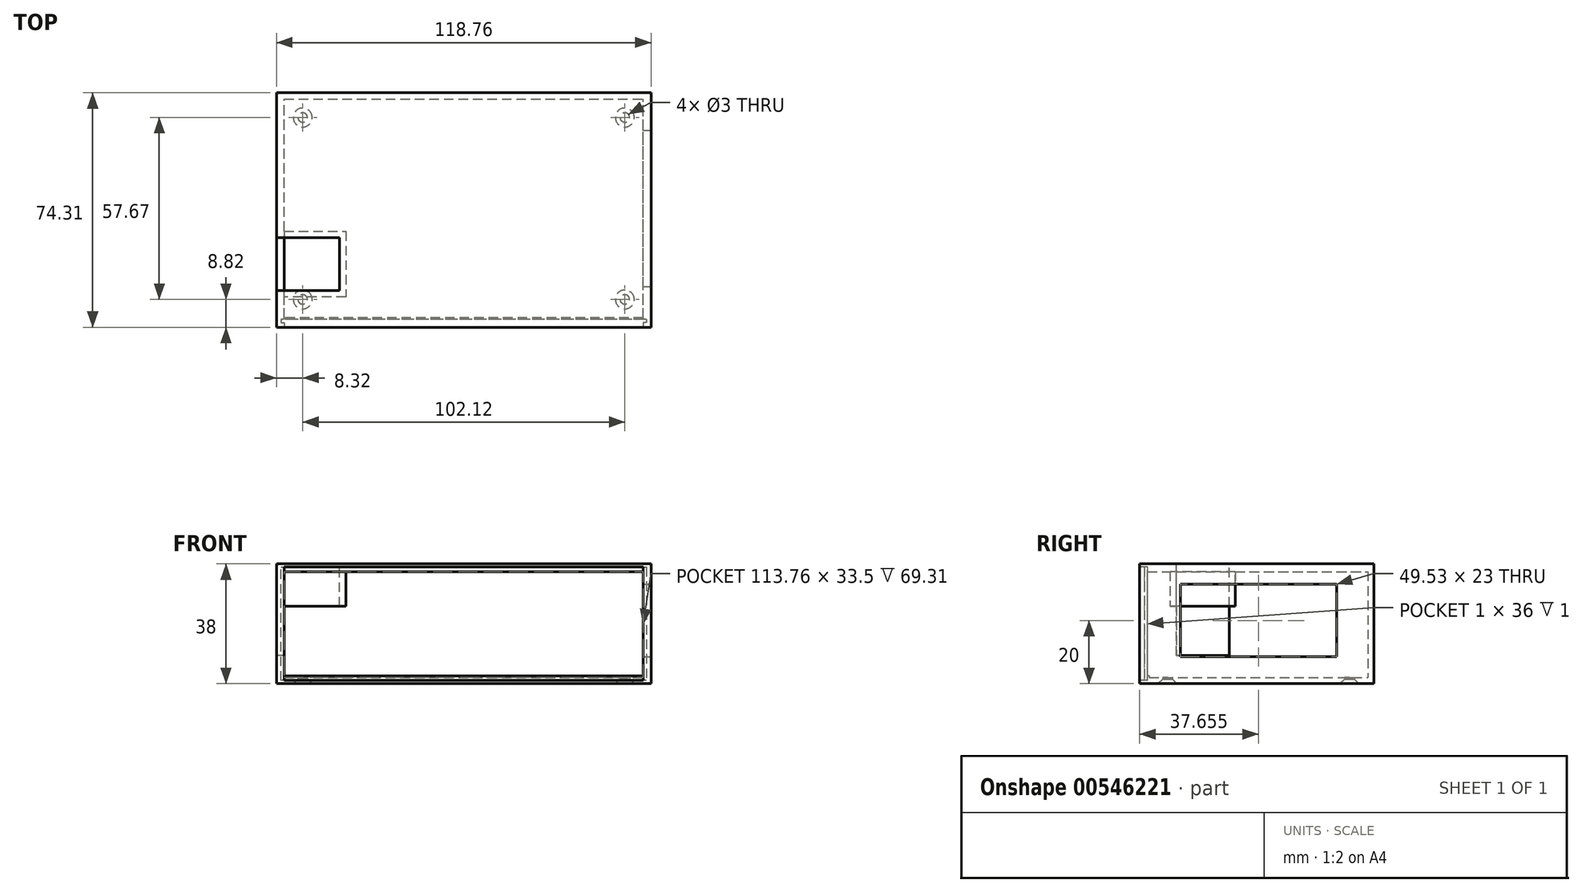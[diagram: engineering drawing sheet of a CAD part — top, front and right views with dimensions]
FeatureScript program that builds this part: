
annotation { "Feature Type Name" : "Feature", "Feature Type Description" : "" }
export const myFeature = defineFeature(function(context is Context, id is Id, definition is map)
    precondition{}
    {
        {
            var Q0;
            Q0=qCreatedBy(makeId("Top.planeOp"),FACE);
            var sketch = newSketch(context, id + "F0", { "sketchPlane" : qUnion([Q0])});
            skLineSegment(sketch, "E0.bottom", {"start": v(0, 0) * mm, "end": v(111.76, 0) * mm, "construction": true});
            skLineSegment(sketch, "E0.top", {"start": v(0, 67.31) * mm, "end": v(111.76, 67.31) * mm, "construction": true});
            skLineSegment(sketch, "E0.left", {"start": v(0, 0) * mm, "end": v(0, 67.3) * mm, "construction": true});
            skLineSegment(sketch, "E0.right", {"start": v(111.76, 0) * mm, "end": v(111.76, 67.3) * mm, "construction": true});
            skLineSegment(sketch, "E1", {"start": v(0, 4.82) * mm, "end": v(4.82, 4.82) * mm, "construction": true});
            skLineSegment(sketch, "E2", {"start": v(4.82, 4.82) * mm, "end": v(4.82, 0) * mm, "construction": true});
            skCircle(sketch, "E3", {"center": v(4.82, 4.82) * mm, "radius": 1.5 * mm});
            skLineSegment(sketch, "E4", {"start": v(0, 33.65) * mm, "end": v(111.76, 33.65) * mm, "construction": true});
            skLineSegment(sketch, "E5", {"start": v(55.88, 67.31) * mm, "end": v(55.88, 0) * mm, "construction": true});
            skCircle(sketch, "E6.MirrorC", {"center": v(4.82, 62.49) * mm, "radius": 1.5 * mm});
            skCircle(sketch, "E7.MirrorC", {"center": v(106.94, 62.5) * mm, "radius": 1.5 * mm});
            skCircle(sketch, "E8.MirrorC", {"center": v(106.94, 4.82) * mm, "radius": 1.5 * mm});
            skLineSegment(sketch, "E9.bottom", {"start": v(-1, -1) * mm, "end": v(112.76, -1) * mm});
            skLineSegment(sketch, "E9.top", {"start": v(-1, 68.31) * mm, "end": v(112.76, 68.31) * mm});
            skLineSegment(sketch, "E9.left", {"start": v(-1, -1) * mm, "end": v(-1, 68.31) * mm});
            skLineSegment(sketch, "E9.right", {"start": v(112.76, -1) * mm, "end": v(112.76, 68.31) * mm});
            skLineSegment(sketch, "E10", {"start": v(0, 0) * mm, "end": v(0, -1) * mm, "construction": true});
            skLineSegment(sketch, "E11", {"start": v(0, 0) * mm, "end": v(-1, 0) * mm, "construction": true});
            skLineSegment(sketch, "E12", {"start": v(0, 67.31) * mm, "end": v(0, 68.31) * mm, "construction": true});
            skLineSegment(sketch, "E13", {"start": v(111.76, 67.31) * mm, "end": v(112.76, 67.31) * mm, "construction": true});
            skLineSegment(sketch, "E14.bottom", {"start": v(-3.5, -4) * mm, "end": v(115.26, -4) * mm});
            skLineSegment(sketch, "E14.top", {"start": v(-3.5, 70.31) * mm, "end": v(115.26, 70.31) * mm});
            skLineSegment(sketch, "E14.left", {"start": v(-3.5, -4) * mm, "end": v(-3.5, 70.31) * mm});
            skLineSegment(sketch, "E14.right", {"start": v(115.26, -4) * mm, "end": v(115.26, 70.31) * mm});
            skLineSegment(sketch, "E15", {"start": v(-1, -1) * mm, "end": v(-1, -4) * mm, "construction": true});
            skLineSegment(sketch, "E16", {"start": v(-1, -1) * mm, "end": v(-3.5, -1) * mm, "construction": true});
            skLineSegment(sketch, "E17", {"start": v(-1, 68.31) * mm, "end": v(-1, 70.31) * mm, "construction": true});
            skLineSegment(sketch, "E18", {"start": v(112.76, 68.31) * mm, "end": v(115.26, 68.31) * mm, "construction": true});
            skCircle(sketch, "E19", {"center": v(4.82, 4.82) * mm, "radius": 3 * mm});
            skCircle(sketch, "E20.MirrorC", {"center": v(4.82, 62.49) * mm, "radius": 3 * mm});
            skCircle(sketch, "E21.MirrorC", {"center": v(106.94, 62.5) * mm, "radius": 3 * mm});
            skCircle(sketch, "E22.MirrorC", {"center": v(106.94, 4.82) * mm, "radius": 3 * mm});
            skSolve(sketch);
        }
        {
            var Q0;
            Q0=makeQuery(id+"F0.imprint","IMPRINT",FACE,{"disambiguationData":[TD([[makeQuery(id+"F0.imprint","IMPRINT",EDGE,{"derivedFrom":sQuery(id+"F0.wireOp",EDGE,"E9.bottom")}),1.0]])]});
            var Q1;
            Q1=makeQuery(id+"F0.imprint","IMPRINT",FACE,{"disambiguationData":[TD([[makeQuery(id+"F0.imprint","IMPRINT",EDGE,{"derivedFrom":sQuery(id+"F0.wireOp",EDGE,"E7.MirrorC")}),-1.0]])]});
            var Q2;
            Q2=makeQuery(id+"F0.imprint","IMPRINT",FACE,{"disambiguationData":[TD([[makeQuery(id+"F0.imprint","IMPRINT",EDGE,{"derivedFrom":sQuery(id+"F0.wireOp",EDGE,"E7.MirrorC")}),1.0]])]});
            var Q3;
            Q3=makeQuery(id+"F0.imprint","IMPRINT",FACE,{"disambiguationData":[TD([[makeQuery(id+"F0.imprint","IMPRINT",EDGE,{"derivedFrom":sQuery(id+"F0.wireOp",EDGE,"E8.MirrorC")}),1.0]])]});
            var Q4;
            Q4=makeQuery(id+"F0.imprint","IMPRINT",FACE,{"disambiguationData":[TD([[makeQuery(id+"F0.imprint","IMPRINT",EDGE,{"derivedFrom":sQuery(id+"F0.wireOp",EDGE,"E8.MirrorC")}),-1.0]])]});
            var Q5;
            Q5=makeQuery(id+"F0.imprint","IMPRINT",FACE,{"disambiguationData":[TD([[makeQuery(id+"F0.imprint","IMPRINT",EDGE,{"derivedFrom":sQuery(id+"F0.wireOp",EDGE,"E3")}),-1.0]])]});
            var Q6;
            Q6=makeQuery(id+"F0.imprint","IMPRINT",FACE,{"disambiguationData":[TD([[makeQuery(id+"F0.imprint","IMPRINT",EDGE,{"derivedFrom":sQuery(id+"F0.wireOp",EDGE,"E3")}),1.0]])]});
            var Q7;
            Q7=makeQuery(id+"F0.imprint","IMPRINT",FACE,{"disambiguationData":[TD([[makeQuery(id+"F0.imprint","IMPRINT",EDGE,{"derivedFrom":sQuery(id+"F0.wireOp",EDGE,"E6.MirrorC")}),1.0]])]});
            var Q8;
            Q8=makeQuery(id+"F0.imprint","IMPRINT",FACE,{"disambiguationData":[TD([[makeQuery(id+"F0.imprint","IMPRINT",EDGE,{"derivedFrom":sQuery(id+"F0.wireOp",EDGE,"E6.MirrorC")}),-1.0]])]});
            extrude(context, id + "F1", {"entities" : qUnion([Q0, Q1, Q2, Q3, Q4, Q5, Q6, Q7, Q8]), "depth" : 2 * mm, "offsetDistance" : 25 * mm});
        }
        {
            var Q0;
            Q0=makeQuery(id+"F0.imprint","IMPRINT",FACE,{"disambiguationData":[TD([[makeQuery(id+"F0.imprint","IMPRINT",EDGE,{"derivedFrom":sQuery(id+"F0.wireOp",EDGE,"E9.bottom")}),-1.0]])]});
            extrude(context, id + "F2", {"entities" : qUnion([Q0]), "operationType" : NewBodyOperationType.ADD, "depth" : 38 * mm, "offsetDistance" : 25 * mm});
        }
        {
            var Q0;
            Q0=makeQuery(id+"F2.opExtrude","SWEPT_FACE",FACE,{"disambiguationData":[OSD([sQuery(id+"F0.wireOp",EDGE,"E14.right")])]});
            var sketch = newSketch(context, id + "F3", { "sketchPlane" : qUnion([Q0])});
            skLineSegment(sketch, "E23.bottom", {"start": v(-4, 38) * mm, "end": v(70.31, 38) * mm});
            skLineSegment(sketch, "E23.top", {"start": v(-4, 0) * mm, "end": v(70.31, 0) * mm});
            skLineSegment(sketch, "E23.left", {"start": v(-4, 38) * mm, "end": v(-4, 0) * mm});
            skLineSegment(sketch, "E23.right", {"start": v(70.31, 38) * mm, "end": v(70.31, 0) * mm});
            skLineSegment(sketch, "E24", {"start": v(0, 0) * mm, "end": v(0, 2.5) * mm, "construction": true});
            skLineSegment(sketch, "E25", {"start": v(0, 2.5) * mm, "end": v(0, 8.5) * mm, "construction": true});
            skLineSegment(sketch, "E26", {"start": v(0, 8.5) * mm, "end": v(8.89, 8.5) * mm, "construction": true});
            skLineSegment(sketch, "E27", {"start": v(0, 8.5) * mm, "end": v(-4, 8.5) * mm, "construction": true});
            skLineSegment(sketch, "E28", {"start": v(8.9, 8.5) * mm, "end": v(8.9, 31.5) * mm});
            skLineSegment(sketch, "E29", {"start": v(8.89, 8.5) * mm, "end": v(58.42, 8.5) * mm});
            skLineSegment(sketch, "E30", {"start": v(58.42, 8.5) * mm, "end": v(67.3, 8.5) * mm, "construction": true});
            skLineSegment(sketch, "E31", {"start": v(67.3, 8.5) * mm, "end": v(70.31, 8.5) * mm, "construction": true});
            skLineSegment(sketch, "E32", {"start": v(8.89, 31.5) * mm, "end": v(58.42, 31.5) * mm});
            skLineSegment(sketch, "E33", {"start": v(58.42, 31.5) * mm, "end": v(58.42, 8.5) * mm});
            skSolve(sketch);
        }
        {
            var Q0;
            Q0=makeQuery(id+"F3.imprint","IMPRINT",FACE,{"disambiguationData":[TD([[makeQuery(id+"F3.imprint","IMPRINT",EDGE,{"derivedFrom":sQuery(id+"F3.wireOp",EDGE,"E28")}),-1.0]])]});
            extrude(context, id + "F4", {"entities" : qUnion([Q0]), "operationType" : NewBodyOperationType.REMOVE, "endBound" : BoundingType.UP_TO_NEXT, "oppositeDirection" : true, "depth" : 25 * mm, "offsetDistance" : 25 * mm});
        }
        {
            var Q0;
            Q0=makeQuery(id+"F2.opExtrude","SWEPT_FACE",FACE,{"disambiguationData":[OSD([sQuery(id+"F0.wireOp",EDGE,"E14.left")])]});
            var sketch = newSketch(context, id + "F5", { "sketchPlane" : qUnion([Q0])});
            skLineSegment(sketch, "E34", {"start": v(0, 0) * mm, "end": v(0, 9) * mm, "construction": true});
            skLineSegment(sketch, "E35", {"start": v(0, 9) * mm, "end": v(-7.62, 9) * mm, "construction": true});
            skLineSegment(sketch, "E36", {"start": v(-7.62, 9) * mm, "end": v(-24.38, 9) * mm});
            skLineSegment(sketch, "E37", {"start": v(-24.38, 9) * mm, "end": v(-24.38, 38) * mm});
            skLineSegment(sketch, "E38.bottom", {"start": v(-70.31, 38) * mm, "end": v(4, 38) * mm});
            skLineSegment(sketch, "E38.top", {"start": v(-70.31, 0) * mm, "end": v(4, 0) * mm});
            skLineSegment(sketch, "E38.left", {"start": v(-70.31, 38) * mm, "end": v(-70.31, 0) * mm});
            skLineSegment(sketch, "E38.right", {"start": v(4, 38) * mm, "end": v(4, 0) * mm});
            skLineSegment(sketch, "E39", {"start": v(-7.62, 9) * mm, "end": v(-7.62, 38) * mm});
            skSolve(sketch);
        }
        {
            var Q0;
            Q0=makeQuery(id+"F5.imprint","IMPRINT",FACE,{"disambiguationData":[TD([[makeQuery(id+"F5.imprint","IMPRINT",EDGE,{"derivedFrom":sQuery(id+"F5.wireOp",EDGE,"E36")}),-1.0]])]});
            extrude(context, id + "F6", {"entities" : qUnion([Q0]), "operationType" : NewBodyOperationType.REMOVE, "endBound" : BoundingType.UP_TO_NEXT, "oppositeDirection" : true, "depth" : 25 * mm, "offsetDistance" : 25 * mm});
        }
        {
            var Q0;
            Q0=makeQuery(id+"F2.opExtrude","CAP_FACE",FACE,{"disambiguationData":[OSD([sQuery(id+"F0.wireOp",EDGE,"E9.bottom"),sQuery(id+"F0.wireOp",EDGE,"E9.top"),sQuery(id+"F0.wireOp",EDGE,"E9.left"),sQuery(id+"F0.wireOp",EDGE,"E9.right"),sQuery(id+"F0.wireOp",EDGE,"E14.bottom"),sQuery(id+"F0.wireOp",EDGE,"E14.top"),sQuery(id+"F0.wireOp",EDGE,"E14.left"),sQuery(id+"F0.wireOp",EDGE,"E14.right")])],"isStart":false});
            var sketch = newSketch(context, id + "F7", { "sketchPlane" : qUnion([Q0])});
            skLineSegment(sketch, "E40.bottom", {"start": v(-1, -1) * mm, "end": v(112.76, -1) * mm});
            skLineSegment(sketch, "E40.top", {"start": v(-1, 68.31) * mm, "end": v(112.76, 68.31) * mm});
            skLineSegment(sketch, "E40.left", {"start": v(-1, -1) * mm, "end": v(-1, 68.31) * mm});
            skLineSegment(sketch, "E40.right", {"start": v(112.76, -1) * mm, "end": v(112.76, 68.31) * mm});
            skLineSegment(sketch, "E41", {"start": v(-1, 24.38) * mm, "end": v(18.5, 24.38) * mm});
            skLineSegment(sketch, "E42", {"start": v(18.5, 24.38) * mm, "end": v(18.5, 7.62) * mm});
            skLineSegment(sketch, "E43", {"start": v(18.5, 7.62) * mm, "end": v(-1, 7.62) * mm});
            skSolve(sketch);
        }
        {
            var Q0;
            {var subQ4=sQuery(id+"F7.wireOp",EDGE,"E40.bottom");Q0=makeQuery(id+"F7.imprint","IMPRINT",FACE,{"disambiguationData":[TD([[makeQuery(id+"F7.imprint","IMPRINT",EDGE,{"derivedFrom":subQ4}),1.0]])]});}
            extrude(context, id + "F8", {"entities" : qUnion([Q0]), "operationType" : NewBodyOperationType.ADD, "oppositeDirection" : true, "depth" : 2.5 * mm, "offsetDistance" : 25 * mm});
        }
        {
            var Q0;
            Q0=makeQuery(id+"F8.boolean.opBoolean","MERGE",FACE,{"derivedFrom":[makeQuery(id+"F6.boolean.opBoolean","COPY",FACE,{"derivedFrom":makeQuery(id+"F6.opExtrude","SWEPT_FACE",FACE,{"disambiguationData":[OSD([sQuery(id+"F5.wireOp",EDGE,"E37")])]})}),makeQuery(id+"F8.opExtrude","SWEPT_FACE",FACE,{"disambiguationData":[OSD([sQuery(id+"F7.wireOp",EDGE,"E41")])]})]});
            var sketch = newSketch(context, id + "F9", { "sketchPlane" : qUnion([Q0])});
            skLineSegment(sketch, "E44", {"start": v(18.5, 35.5) * mm, "end": v(-1, 35.5) * mm});
            skLineSegment(sketch, "E45", {"start": v(-1, 35.5) * mm, "end": v(-1, 24.5) * mm});
            skLineSegment(sketch, "E46", {"start": v(-1, 24.5) * mm, "end": v(18.5, 24.5) * mm});
            skLineSegment(sketch, "E47", {"start": v(18.5, 24.5) * mm, "end": v(18.5, 35.5) * mm});
            skSolve(sketch);
        }
        {
            var Q0;
            Q0=makeQuery(id+"F9.imprint","IMPRINT",FACE,{"disambiguationData":[TD([[makeQuery(id+"F9.imprint","IMPRINT",EDGE,{"derivedFrom":sQuery(id+"F9.wireOp",EDGE,"E44")}),-1.0]])]});
            extrude(context, id + "F10", {"entities" : qUnion([Q0]), "operationType" : NewBodyOperationType.ADD, "oppositeDirection" : true, "depth" : 2 * mm, "offsetDistance" : 25 * mm});
        }
        {
            var Q0;
            Q0=makeQuery(id+"F8.boolean.opBoolean","MERGE",FACE,{"derivedFrom":[makeQuery(id+"F6.boolean.opBoolean","COPY",FACE,{"derivedFrom":makeQuery(id+"F6.opExtrude","SWEPT_FACE",FACE,{"disambiguationData":[OSD([sQuery(id+"F5.wireOp",EDGE,"E39")])]})}),makeQuery(id+"F8.opExtrude","SWEPT_FACE",FACE,{"disambiguationData":[OSD([sQuery(id+"F7.wireOp",EDGE,"E43")])]})]});
            var sketch = newSketch(context, id + "F11", { "sketchPlane" : qUnion([Q0])});
            skLineSegment(sketch, "E48", {"start": v(-18.5, 35.5) * mm, "end": v(-18.5, 24.5) * mm});
            skLineSegment(sketch, "E49", {"start": v(-18.5, 24.5) * mm, "end": v(1, 24.5) * mm});
            skLineSegment(sketch, "E50", {"start": v(1, 24.5) * mm, "end": v(1, 35.5) * mm});
            skLineSegment(sketch, "E51", {"start": v(1, 35.5) * mm, "end": v(-18.5, 35.5) * mm});
            skSolve(sketch);
        }
        {
            var Q0;
            Q0=makeQuery(id+"F11.imprint","IMPRINT",FACE,{"disambiguationData":[TD([[makeQuery(id+"F11.imprint","IMPRINT",EDGE,{"derivedFrom":sQuery(id+"F11.wireOp",EDGE,"E48")}),1.0]])]});
            extrude(context, id + "F12", {"entities" : qUnion([Q0]), "operationType" : NewBodyOperationType.ADD, "oppositeDirection" : true, "depth" : 2 * mm, "offsetDistance" : 25 * mm});
        }
        {
            var Q0;
            Q0=makeQuery(id+"F8.opExtrude","SWEPT_FACE",FACE,{"disambiguationData":[OSD([sQuery(id+"F7.wireOp",EDGE,"E42")])]});
            var sketch = newSketch(context, id + "F13", { "sketchPlane" : qUnion([Q0])});
            skLineSegment(sketch, "E52.bottom", {"start": v(-24.38, 38) * mm, "end": v(-7.62, 38) * mm});
            skLineSegment(sketch, "E52.top", {"start": v(-24.38, 24.5) * mm, "end": v(-7.62, 24.5) * mm});
            skLineSegment(sketch, "E52.left", {"start": v(-24.38, 38) * mm, "end": v(-24.38, 24.5) * mm});
            skLineSegment(sketch, "E52.right", {"start": v(-7.62, 38) * mm, "end": v(-7.62, 24.5) * mm});
            skSolve(sketch);
        }
        {
            var Q0;
            Q0=qSketchRegion(id+"F13",true);
            extrude(context, id + "F14", {"entities" : qUnion([Q0]), "operationType" : NewBodyOperationType.ADD, "depth" : 2 * mm, "offsetDistance" : 25 * mm});
        }
        {
            var Q0;
            Q0=makeQuery(id+"F2.opExtrude","SWEPT_FACE",FACE,{"disambiguationData":[OSD([sQuery(id+"F0.wireOp",EDGE,"E14.bottom")])]});
            var sketch = newSketch(context, id + "F15", { "sketchPlane" : qUnion([Q0])});
            skLineSegment(sketch, "E53.bottom", {"start": v(-3.5, 0) * mm, "end": v(115.26, 0) * mm});
            skLineSegment(sketch, "E53.top", {"start": v(-3.5, 38) * mm, "end": v(115.26, 38) * mm});
            skLineSegment(sketch, "E53.left", {"start": v(-3.5, 0) * mm, "end": v(-3.5, 38) * mm});
            skLineSegment(sketch, "E53.right", {"start": v(115.26, 0) * mm, "end": v(115.26, 38) * mm});
            skLineSegment(sketch, "E54", {"start": v(-1, 37) * mm, "end": v(-1, 38) * mm, "construction": true});
            skLineSegment(sketch, "E55", {"start": v(-1, 37) * mm, "end": v(-3.5, 37) * mm, "construction": true});
            skLineSegment(sketch, "E56", {"start": v(115.26, 1) * mm, "end": v(112.76, 1) * mm, "construction": true});
            skLineSegment(sketch, "E57", {"start": v(112.76, 1) * mm, "end": v(112.76, 0) * mm, "construction": true});
            skLineSegment(sketch, "E58.bottom", {"start": v(-1, 37) * mm, "end": v(112.76, 37) * mm});
            skLineSegment(sketch, "E58.top", {"start": v(-1, 1) * mm, "end": v(112.76, 1) * mm});
            skLineSegment(sketch, "E58.left", {"start": v(-1, 37) * mm, "end": v(-1, 1) * mm});
            skLineSegment(sketch, "E58.right", {"start": v(112.76, 37) * mm, "end": v(112.76, 1) * mm});
            skLineSegment(sketch, "E59", {"start": v(112.76, 2.5) * mm, "end": v(-1, 2.5) * mm});
            skLineSegment(sketch, "E60", {"start": v(112.76, 35.5) * mm, "end": v(-1, 35.5) * mm});
            skSolve(sketch);
        }
        {
            var Q0;
            {var subQ0=sQuery(id+"F15.wireOp",EDGE,"E59");Q0=makeQuery(id+"F15.imprint","IMPRINT",FACE,{"disambiguationData":[TD([[makeQuery(id+"F15.imprint","IMPRINT",EDGE,{"derivedFrom":subQ0}),-1.0]])]});}
            extrude(context, id + "F16", {"entities" : qUnion([Q0]), "operationType" : NewBodyOperationType.REMOVE, "endBound" : BoundingType.UP_TO_NEXT, "oppositeDirection" : true, "depth" : 25 * mm, "offsetDistance" : 25 * mm});
        }
        {
            var Q0;
            Q0=makeQuery(id+"F2.opExtrude","SWEPT_FACE",FACE,{"disambiguationData":[OSD([sQuery(id+"F0.wireOp",EDGE,"E14.bottom")])]});
            var sketch = newSketch(context, id + "F17", { "sketchPlane" : qUnion([Q0])});
            skLineSegment(sketch, "E61.bottom", {"start": v(-1, 35.5) * mm, "end": v(112.76, 35.5) * mm});
            skLineSegment(sketch, "E61.top", {"start": v(-1, 2.5) * mm, "end": v(112.76, 2.5) * mm});
            skLineSegment(sketch, "E61.left", {"start": v(-1, 35.5) * mm, "end": v(-1, 2.5) * mm});
            skLineSegment(sketch, "E61.right", {"start": v(112.76, 35.5) * mm, "end": v(112.76, 2.5) * mm});
            skLineSegment(sketch, "E62", {"start": v(112.76, 2.5) * mm, "end": v(112.76, 1) * mm});
            skLineSegment(sketch, "E63", {"start": v(112.76, 1) * mm, "end": v(-1, 1) * mm});
            skLineSegment(sketch, "E64", {"start": v(-1, 1) * mm, "end": v(-1, 2.5) * mm});
            skLineSegment(sketch, "E65", {"start": v(-1, 35.5) * mm, "end": v(-1, 37) * mm});
            skLineSegment(sketch, "E66", {"start": v(-1, 37) * mm, "end": v(112.76, 37) * mm});
            skLineSegment(sketch, "E67", {"start": v(112.76, 37) * mm, "end": v(112.76, 35.5) * mm});
            skSolve(sketch);
        }
        {
            var Q0;
            Q0=makeQuery(id+"F17.imprint","IMPRINT",FACE,{"disambiguationData":[TD([[makeQuery(id+"F17.imprint","IMPRINT",EDGE,{"derivedFrom":sQuery(id+"F17.wireOp",EDGE,"E61.bottom")}),-1.0]])]});
            var Q1;
            Q1=makeQuery(id+"F17.imprint","IMPRINT",FACE,{"disambiguationData":[TD([[makeQuery(id+"F17.imprint","IMPRINT",EDGE,{"derivedFrom":sQuery(id+"F17.wireOp",EDGE,"E61.top")}),1.0]])]});
            extrude(context, id + "F18", {"entities" : qUnion([Q0, Q1]), "operationType" : NewBodyOperationType.REMOVE, "oppositeDirection" : true, "depth" : 2.5 * mm, "offsetDistance" : 25 * mm});
        }
        {
            var Q0;
            Q0=makeQuery(id+"F18.boolean.opBoolean","MERGE",FACE,{"derivedFrom":[makeQuery(id+"F16.boolean.opBoolean","MERGE",FACE,{"derivedFrom":[makeQuery(id+"F2.opExtrude","SWEPT_FACE",FACE,{"disambiguationData":[OSD([sQuery(id+"F0.wireOp",EDGE,"E9.left")])]}),makeQuery(id+"F16.opExtrude","SWEPT_FACE",FACE,{"disambiguationData":[OSD([sQuery(id+"F15.wireOp",EDGE,"E58.left")])]})]}),makeQuery(id+"F18.opExtrude","SWEPT_FACE",FACE,{"disambiguationData":[OSD([sQuery(id+"F17.wireOp",EDGE,"E64")])]}),makeQuery(id+"F18.opExtrude","SWEPT_FACE",FACE,{"disambiguationData":[OSD([sQuery(id+"F17.wireOp",EDGE,"E65")])]})]});
            var sketch = newSketch(context, id + "F19", { "sketchPlane" : qUnion([Q0])});
            skLineSegment(sketch, "E68", {"start": v(-1.5, 37) * mm, "end": v(-2.5, 37) * mm});
            skLineSegment(sketch, "E69", {"start": v(-1.5, 1) * mm, "end": v(-1.5, 37) * mm});
            skLineSegment(sketch, "E70", {"start": v(-1.5, 1) * mm, "end": v(-2.5, 1) * mm});
            skLineSegment(sketch, "E71", {"start": v(-2.5, 1) * mm, "end": v(-2.5, 37) * mm});
            skSolve(sketch);
        }
        {
            var Q0;
            {var subQ4=sQuery(id+"F19.wireOp",EDGE,"E68");Q0=makeQuery(id+"F19.imprint","IMPRINT",FACE,{"disambiguationData":[TD([[makeQuery(id+"F19.imprint","IMPRINT",EDGE,{"derivedFrom":subQ4}),1.0]])]});}
            extrude(context, id + "F20", {"entities" : qUnion([Q0]), "operationType" : NewBodyOperationType.REMOVE, "oppositeDirection" : true, "depth" : 1 * mm, "offsetDistance" : 25 * mm});
        }
        {
            var Q0;
            Q0=makeQuery(id+"F18.boolean.opBoolean","MERGE",FACE,{"derivedFrom":[makeQuery(id+"F16.boolean.opBoolean","MERGE",FACE,{"derivedFrom":[makeQuery(id+"F2.opExtrude","SWEPT_FACE",FACE,{"disambiguationData":[OSD([sQuery(id+"F0.wireOp",EDGE,"E9.right")])]}),makeQuery(id+"F16.opExtrude","SWEPT_FACE",FACE,{"disambiguationData":[OSD([sQuery(id+"F15.wireOp",EDGE,"E58.right")])]})]}),makeQuery(id+"F18.opExtrude","SWEPT_FACE",FACE,{"disambiguationData":[OSD([sQuery(id+"F17.wireOp",EDGE,"E62")])]}),makeQuery(id+"F18.opExtrude","SWEPT_FACE",FACE,{"disambiguationData":[OSD([sQuery(id+"F17.wireOp",EDGE,"E67")])]})]});
            var sketch = newSketch(context, id + "F21", { "sketchPlane" : qUnion([Q0])});
            skLineSegment(sketch, "E72", {"start": v(1.5, 37) * mm, "end": v(1.5, 1) * mm});
            skLineSegment(sketch, "E73", {"start": v(1.5, 1) * mm, "end": v(2.5, 1) * mm});
            skLineSegment(sketch, "E74", {"start": v(1.5, 37) * mm, "end": v(2.5, 37) * mm});
            skLineSegment(sketch, "E75", {"start": v(2.5, 37) * mm, "end": v(2.5, 1) * mm});
            skSolve(sketch);
        }
        {
            var Q0;
            {var subQ0=sQuery(id+"F21.wireOp",EDGE,"E73");Q0=makeQuery(id+"F21.imprint","IMPRINT",FACE,{"disambiguationData":[TD([[makeQuery(id+"F21.imprint","IMPRINT",EDGE,{"derivedFrom":subQ0}),1.0]])]});}
            extrude(context, id + "F22", {"entities" : qUnion([Q0]), "operationType" : NewBodyOperationType.REMOVE, "oppositeDirection" : true, "depth" : 1 * mm, "offsetDistance" : 25 * mm});
        }
        {
            var Q0;
            Q0=sQuery(id+"F0.wireOp",VERTEX,"E2.start");
            var Q1;
            Q1=sQuery(id+"F0.wireOp",VERTEX,"E8.MirrorC.center");
            var Q2;
            Q2=sQuery(id+"F0.wireOp",VERTEX,"E7.MirrorC.center");
            var Q3;
            Q3=sQuery(id+"F0.wireOp",VERTEX,"E6.MirrorC.center");
            var Q4;
            Q4=makeQuery(id+"F1.opExtrude","SWEPT_BODY",BODY,{"disambiguationData":[OSD([sQuery(id+"F0.wireOp",EDGE,"E9.bottom"),sQuery(id+"F0.wireOp",EDGE,"E9.top"),sQuery(id+"F0.wireOp",EDGE,"E9.left"),sQuery(id+"F0.wireOp",EDGE,"E9.right")])]});
            hole(context, id + "F23", {"style" : HoleStyle.C_SINK, "endStyle" : HoleEndStyle.BLIND, "oppositeDirection" : true, "holeDiameter" : 3 * mm, "cSinkDiameter" : 6 * mm, "cSinkAngle" : 90 * degree, "holeDepth" : 5 * mm, "isTappedThrough" : true, "tappedDepth" : 12 * mm, "tapClearance" : 3, "locations" : qUnion([Q0, Q1, Q2, Q3]), "scope" : qUnion([Q4])});
        }
    });
